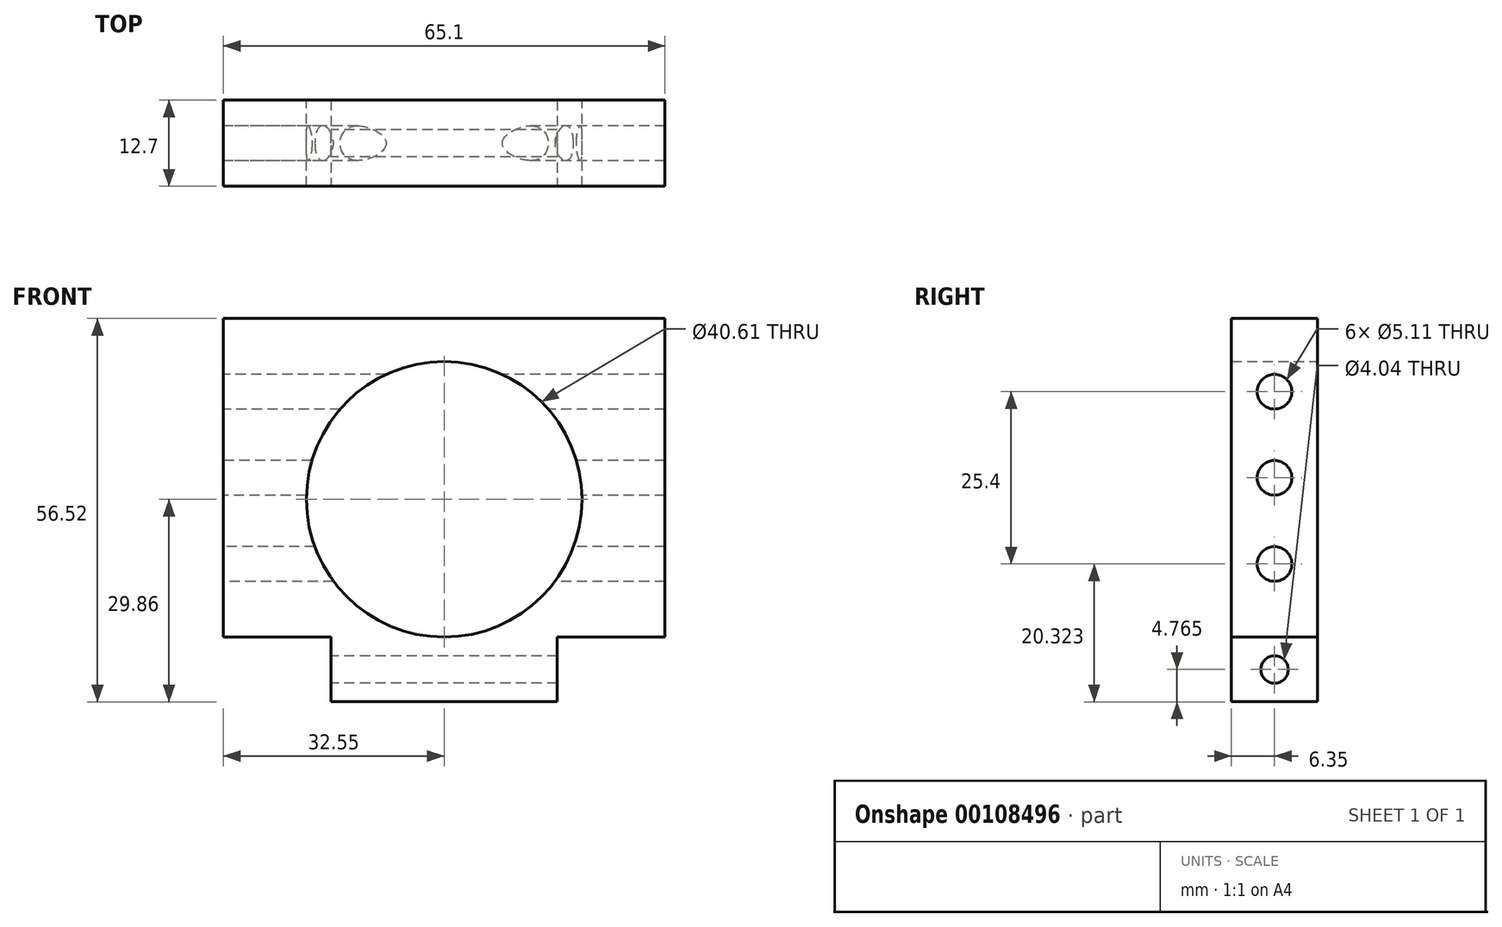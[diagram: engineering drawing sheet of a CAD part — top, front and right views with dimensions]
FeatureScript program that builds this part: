
annotation { "Feature Type Name" : "Feature", "Feature Type Description" : "" }
export const myFeature = defineFeature(function(context is Context, id is Id, definition is map)
    precondition{}
    {
        {
            var Q0;
            Q0=qCreatedBy(makeId("Front.planeOp"),FACE);
            var sketch = newSketch(context, id + "F0", { "sketchPlane" : qUnion([Q0])});
            skLineSegment(sketch, "E0.bottom", {"start": v(32.55, 28.26) * mm, "end": v(-32.55, 28.26) * mm});
            skLineSegment(sketch, "E0.top", {"start": v(32.55, -28.26) * mm, "end": v(-32.55, -28.26) * mm});
            skLineSegment(sketch, "E0.left", {"start": v(32.55, 28.26) * mm, "end": v(32.55, -28.26) * mm});
            skLineSegment(sketch, "E0.right", {"start": v(-32.55, 28.26) * mm, "end": v(-32.55, -28.26) * mm});
            skCircle(sketch, "E1", {"center": v(0, 1.6) * mm, "radius": 20.3 * mm});
            skSolve(sketch);
        }
        {
            var Q0;
            Q0=makeQuery(id+"F0.imprint","IMPRINT",FACE,{"disambiguationData":[TD([[makeQuery(id+"F0.imprint","IMPRINT",EDGE,{"derivedFrom":sQuery(id+"F0.wireOp",EDGE,"E0.bottom")}),1.0]])]});
            extrude(context, id + "F1", {"entities" : qUnion([Q0]), "depth" : 12.7 * mm});
        }
        {
            var Q0;
            Q0=makeQuery(id+"F1.opExtrude","CAP_FACE",FACE,{"disambiguationData":[OSD([sQuery(id+"F0.wireOp",EDGE,"E0.bottom"),sQuery(id+"F0.wireOp",EDGE,"E0.top"),sQuery(id+"F0.wireOp",EDGE,"E0.left"),sQuery(id+"F0.wireOp",EDGE,"E0.right"),sQuery(id+"F0.wireOp",EDGE,"hNUmTCXz-RMn9-OxVv-nieb-AeJgz8Ox1uQo")])],"isStart":false});
            var sketch = newSketch(context, id + "F2", { "sketchPlane" : qUnion([Q0])});
            skLineSegment(sketch, "E2.bottom", {"start": v(32.55, -28.26) * mm, "end": v(16.68, -28.26) * mm});
            skLineSegment(sketch, "E2.top", {"start": v(32.55, -18.73) * mm, "end": v(16.68, -18.73) * mm});
            skLineSegment(sketch, "E2.left", {"start": v(32.55, -28.26) * mm, "end": v(32.55, -18.73) * mm});
            skLineSegment(sketch, "E2.right", {"start": v(16.68, -28.26) * mm, "end": v(16.68, -18.73) * mm});
            skLineSegment(sketch, "E3.MirrorCS", {"start": v(-16.68, -28.26) * mm, "end": v(-16.68, -18.73) * mm});
            skLineSegment(sketch, "E4.MirrorCS", {"start": v(-32.55, -28.26) * mm, "end": v(-16.68, -28.26) * mm});
            skLineSegment(sketch, "E5.MirrorCS", {"start": v(-32.55, -18.73) * mm, "end": v(-16.68, -18.73) * mm});
            skLineSegment(sketch, "E6.MirrorCS", {"start": v(-32.55, -28.26) * mm, "end": v(-32.55, -18.73) * mm});
            skSolve(sketch);
        }
        {
            var Q0;
            Q0=makeQuery(id+"F2.imprint","IMPRINT",FACE,{"disambiguationData":[TD([[makeQuery(id+"F2.imprint","IMPRINT",EDGE,{"derivedFrom":sQuery(id+"F2.wireOp",EDGE,"E4.MirrorCS")}),-1.0]])]});
            var Q1;
            Q1=makeQuery(id+"F2.imprint","IMPRINT",FACE,{"disambiguationData":[TD([[makeQuery(id+"F2.imprint","IMPRINT",EDGE,{"derivedFrom":sQuery(id+"F2.wireOp",EDGE,"E2.bottom")}),-1.0]])]});
            extrude(context, id + "F3", {"entities" : qUnion([Q0, Q1]), "operationType" : NewBodyOperationType.REMOVE, "endBound" : BoundingType.THROUGH_ALL, "oppositeDirection" : true, "depth" : 25.4 * mm});
        }
        {
            var Q0;
            Q0=makeQuery(id+"F1.opExtrude","SWEPT_FACE",FACE,{"disambiguationData":[OSD([sQuery(id+"F0.wireOp",EDGE,"E0.right")])]});
            var sketch = newSketch(context, id + "F4", { "sketchPlane" : qUnion([Q0])});
            skCircle(sketch, "E7", {"center": v(6.35, 17.46) * mm, "radius": 2.55 * mm});
            skCircle(sketch, "E8", {"center": v(6.35, -7.94) * mm, "radius": 2.55 * mm});
            skCircle(sketch, "E9", {"center": v(6.35, 4.76) * mm, "radius": 2.55 * mm});
            skSolve(sketch);
        }
        {
            var Q0;
            Q0=makeQuery(id+"F4.imprint","IMPRINT",FACE,{"disambiguationData":[TD([[makeQuery(id+"F4.imprint","IMPRINT",EDGE,{"derivedFrom":sQuery(id+"F4.wireOp",EDGE,"E7")}),1.0]])]});
            var Q1;
            Q1=makeQuery(id+"F4.imprint","IMPRINT",FACE,{"disambiguationData":[TD([[makeQuery(id+"F4.imprint","IMPRINT",EDGE,{"derivedFrom":sQuery(id+"F4.wireOp",EDGE,"E8")}),1.0]])]});
            var Q2;
            Q2=makeQuery(id+"F4.imprint","IMPRINT",FACE,{"disambiguationData":[TD([[makeQuery(id+"F4.imprint","IMPRINT",EDGE,{"derivedFrom":sQuery(id+"F4.wireOp",EDGE,"E9")}),1.0]])]});
            extrude(context, id + "F5", {"entities" : qUnion([Q0, Q1, Q2]), "operationType" : NewBodyOperationType.REMOVE, "endBound" : BoundingType.THROUGH_ALL, "oppositeDirection" : true, "depth" : 19.05 * mm});
        }
        {
            var Q0;
            Q0=makeQuery(id+"F3.boolean.opBoolean","COPY",FACE,{"derivedFrom":makeQuery(id+"F3.opExtrude","SWEPT_FACE",FACE,{"disambiguationData":[OSD([sQuery(id+"F2.wireOp",EDGE,"E3.MirrorCS")])]})});
            var sketch = newSketch(context, id + "F6", { "sketchPlane" : qUnion([Q0])});
            skCircle(sketch, "E10", {"center": v(6.35, -23.5) * mm, "radius": 2.02 * mm});
            skSolve(sketch);
        }
        {
            var Q0;
            Q0=makeQuery(id+"F6.imprint","IMPRINT",FACE,{"disambiguationData":[TD([[makeQuery(id+"F6.imprint","IMPRINT",EDGE,{"derivedFrom":sQuery(id+"F6.wireOp",EDGE,"E10")}),1.0]])]});
            extrude(context, id + "F7", {"entities" : qUnion([Q0]), "operationType" : NewBodyOperationType.REMOVE, "endBound" : BoundingType.THROUGH_ALL, "oppositeDirection" : true, "depth" : 25.4 * mm});
        }
    });
